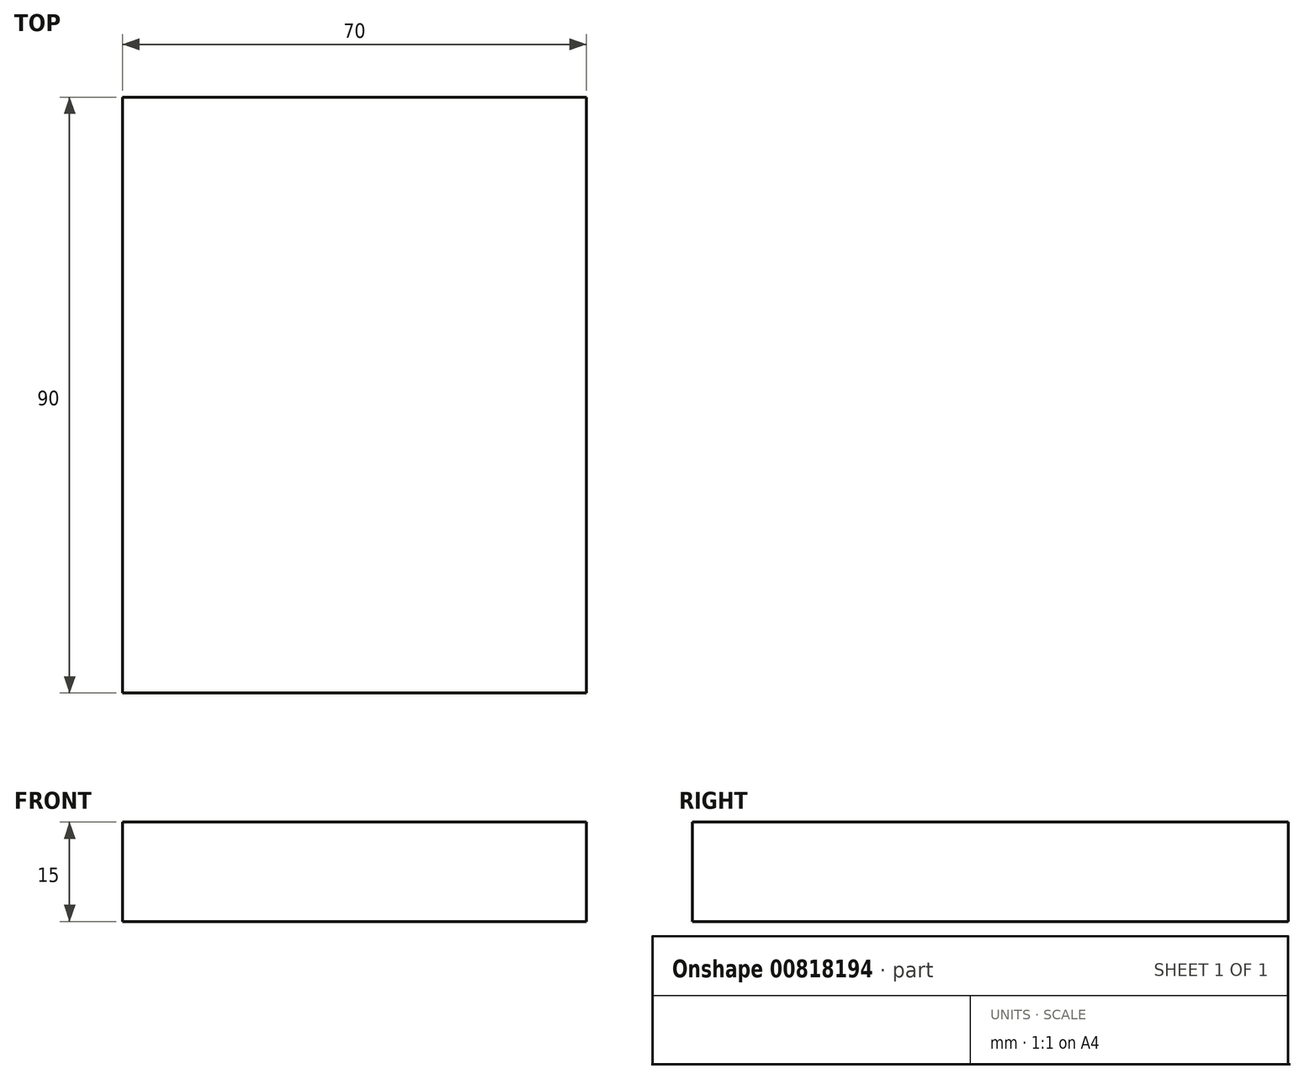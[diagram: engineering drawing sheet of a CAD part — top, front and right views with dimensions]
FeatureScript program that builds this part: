
annotation { "Feature Type Name" : "Feature", "Feature Type Description" : "" }
export const myFeature = defineFeature(function(context is Context, id is Id, definition is map)
    precondition{}
    {
        {
            var Q0;
            Q0=qCreatedBy(makeId("Top.planeOp"),FACE);
            var sketch = newSketch(context, id + "F0", { "sketchPlane" : qUnion([Q0])});
            skLineSegment(sketch, "E0.bottom", {"start": v(0, 0) * mm, "end": v(70, 0) * mm});
            skLineSegment(sketch, "E0.top", {"start": v(0, -90) * mm, "end": v(70, -90) * mm});
            skLineSegment(sketch, "E0.left", {"start": v(0, 0) * mm, "end": v(0, -90) * mm});
            skLineSegment(sketch, "E0.right", {"start": v(70, 0) * mm, "end": v(70, -90) * mm});
            skSolve(sketch);
        }
        {
            var Q0;
            Q0=makeQuery(id+"F0.imprint","IMPRINT",FACE,{"disambiguationData":[TD([[makeQuery(id+"F0.imprint","IMPRINT",EDGE,{"derivedFrom":sQuery(id+"F0.wireOp",EDGE,"E0.bottom")}),-1.0]])]});
            extrude(context, id + "F1", {"entities" : qUnion([Q0]), "depth" : 15 * mm, "offsetDistance" : 25 * mm});
        }
    });
